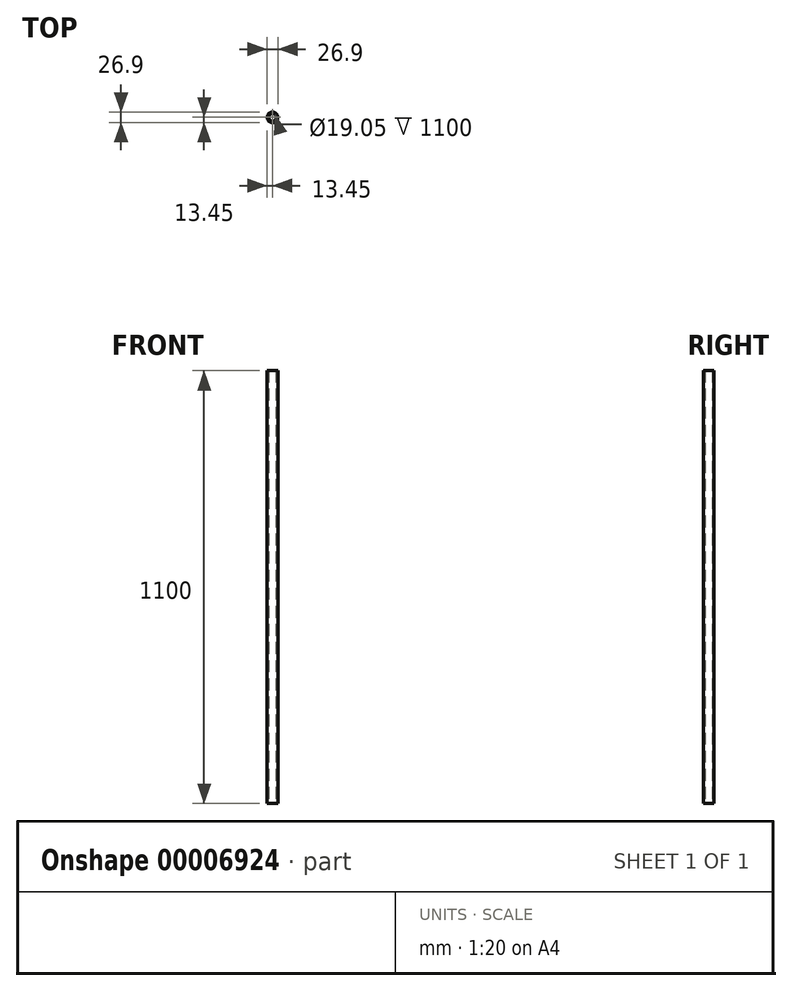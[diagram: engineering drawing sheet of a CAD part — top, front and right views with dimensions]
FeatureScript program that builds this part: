
annotation { "Feature Type Name" : "Feature", "Feature Type Description" : "" }
export const myFeature = defineFeature(function(context is Context, id is Id, definition is map)
    precondition{}
    {
        {
            var Q0;
            Q0=qCreatedBy(makeId("Top.planeOp"),FACE);
            var sketch = newSketch(context, id + "F0", { "sketchPlane" : qUnion([Q0])});
            skCircle(sketch, "E0", {"center": v(0, 0) * mm, "radius": 13.45 * mm});
            skCircle(sketch, "E1", {"center": v(0, 0) * mm, "radius": 9.53 * mm});
            skSolve(sketch);
        }
        {
            var Q0;
            Q0=qSketchRegion(id+"F0",true);
            extrude(context, id + "F1", {"entities" : qUnion([Q0]), "depth" : (1100) * mm});
        }
    });
